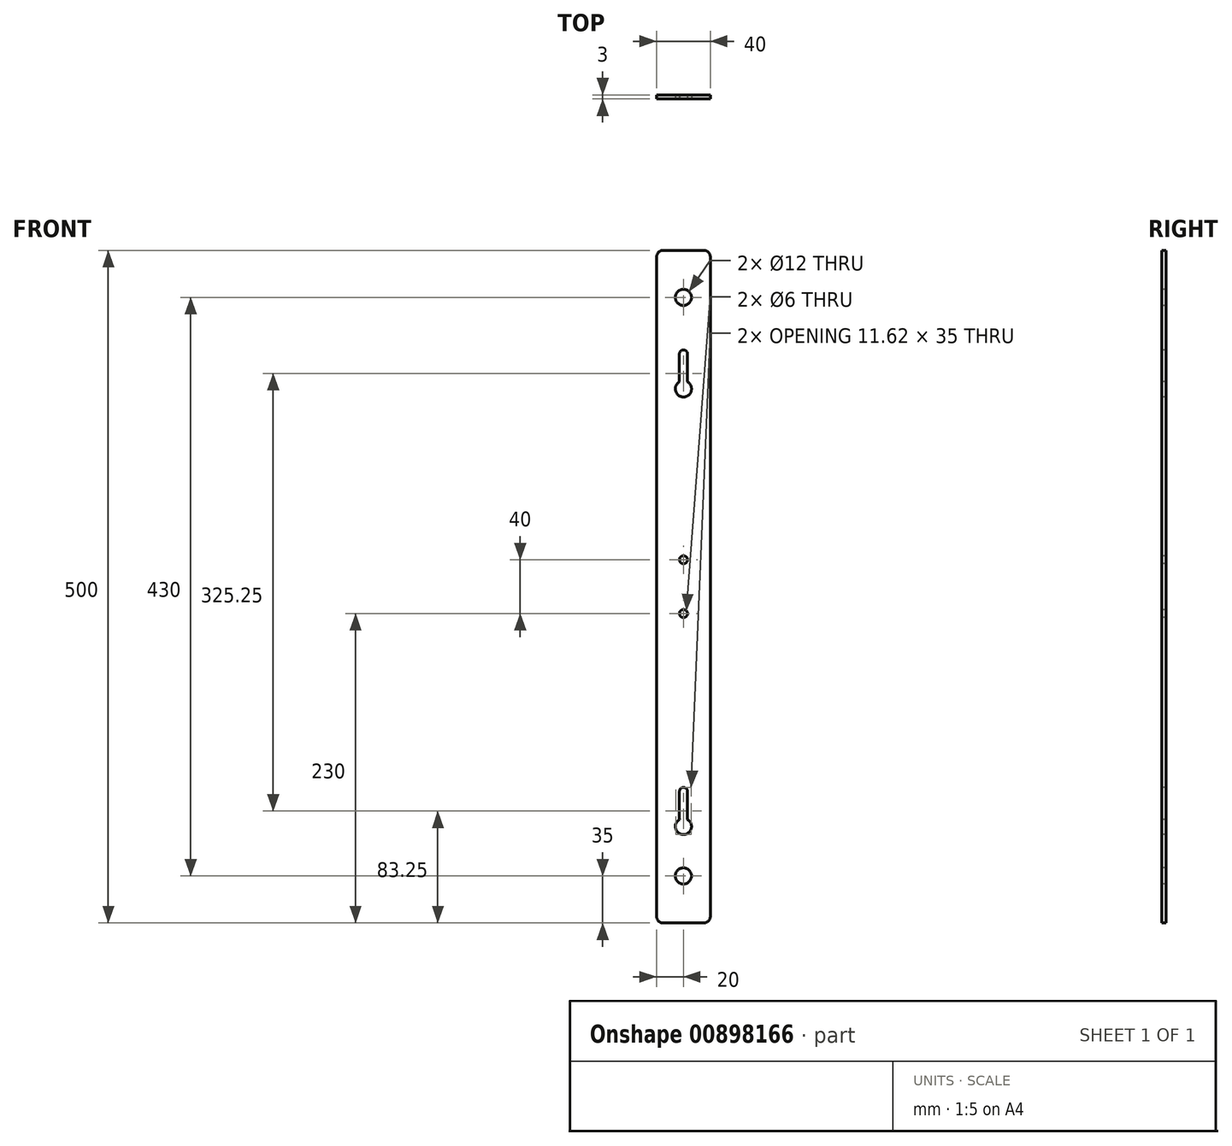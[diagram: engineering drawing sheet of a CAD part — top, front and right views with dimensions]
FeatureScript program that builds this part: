
annotation { "Feature Type Name" : "Feature", "Feature Type Description" : "" }
export const myFeature = defineFeature(function(context is Context, id is Id, definition is map)
    precondition{}
    {
        {
            var Q0;
            Q0=qCreatedBy(makeId("Front.planeOp"),FACE);
            var sketch = newSketch(context, id + "F0", { "sketchPlane" : qUnion([Q0])});
            skLineSegment(sketch, "E0.bottom", {"start": v(-20, 250) * mm, "end": v(20, 250) * mm});
            skLineSegment(sketch, "E0.top", {"start": v(-20, -250) * mm, "end": v(20, -250) * mm});
            skLineSegment(sketch, "E0.left", {"start": v(-20, 250) * mm, "end": v(-20, -250) * mm});
            skLineSegment(sketch, "E0.right", {"start": v(20, 250) * mm, "end": v(20, -250) * mm});
            skPoint(sketch, "E0.middle", {"position": v(0, 0) * mm});
            skSolve(sketch);
        }
        {
            var Q0;
            Q0 = qSketchRegion(id + "F0", true);
            extrude(context, id + "F1", {"entities" : qUnion([Q0]), "depth" : 3 * mm, "offsetDistance" : 25 * mm});
        }
        {
            var Q0;
            Q0=makeQuery(id+"F1.opExtrude","CAP_FACE",FACE,{"disambiguationData":[OSD([sQuery(id+"F0.wireOp",EDGE,"E0.bottom"),sQuery(id+"F0.wireOp",EDGE,"E0.top"),sQuery(id+"F0.wireOp",EDGE,"E0.left"),sQuery(id+"F0.wireOp",EDGE,"E0.right")])],"isStart":false});
            var sketch = newSketch(context, id + "F2", { "sketchPlane" : qUnion([Q0])});
            skPoint(sketch, "E1", {"position": v(0, 215) * mm});
            skPoint(sketch, "E2.MirrorP", {"position": v(0, -215) * mm});
            skSolve(sketch);
        }
        {
            var Q0;
            Q0=sQuery(id+"F2.wireOp",VERTEX,"E2.MirrorP");
            var Q1;
            Q1=sQuery(id+"F2.wireOp",VERTEX,"E1");
            var Q2;
            Q2=makeQuery(id+"F1.opExtrude","SWEPT_BODY",BODY,{"disambiguationData":[OSD([sQuery(id+"F0.wireOp",EDGE,"E0.bottom"),sQuery(id+"F0.wireOp",EDGE,"E0.top"),sQuery(id+"F0.wireOp",EDGE,"E0.left"),sQuery(id+"F0.wireOp",EDGE,"E0.right")])]});
            hole(context, id + "F3", {"style" : HoleStyle.SIMPLE, "endStyle" : HoleEndStyle.THROUGH, "holeDiameter" : 12 * mm, "majorDiameter" : 5 * mm, "isTappedThrough" : true, "tappedDepth" : 12 * mm, "tapClearance" : 3, "startFromSketch" : true, "locations" : qUnion([Q0, Q1]), "scope" : qUnion([Q2])});
        }
        {
            var Q0;
            Q0=makeQuery(id+"F1.opExtrude","CAP_FACE",FACE,{"disambiguationData":[OSD([sQuery(id+"F0.wireOp",EDGE,"E0.bottom"),sQuery(id+"F0.wireOp",EDGE,"E0.top"),sQuery(id+"F0.wireOp",EDGE,"E0.left"),sQuery(id+"F0.wireOp",EDGE,"E0.right")])],"isStart":false});
            var sketch = newSketch(context, id + "F4", { "sketchPlane" : qUnion([Q0])});
            skPoint(sketch, "E3", {"position": v(0, 147) * mm});
            skSolve(sketch);
        }
        {
            var Q0;
            Q0=sQuery(id+"F4.wireOp",VERTEX,"E3");
            var Q1;
            Q1=makeQuery(id+"F1.opExtrude","SWEPT_BODY",BODY,{"disambiguationData":[OSD([sQuery(id+"F0.wireOp",EDGE,"E0.bottom"),sQuery(id+"F0.wireOp",EDGE,"E0.top"),sQuery(id+"F0.wireOp",EDGE,"E0.left"),sQuery(id+"F0.wireOp",EDGE,"E0.right")])]});
            hole(context, id + "F5", {"style" : HoleStyle.SIMPLE, "endStyle" : HoleEndStyle.THROUGH, "holeDiameter" : 12 * mm, "majorDiameter" : 5 * mm, "isTappedThrough" : true, "tappedDepth" : 12 * mm, "tapClearance" : 3, "startFromSketch" : true, "locations" : qUnion([Q0]), "scope" : qUnion([Q1])});
        }
        {
            var Q0;
            Q0=makeQuery(id+"F1.opExtrude","CAP_FACE",FACE,{"disambiguationData":[OSD([sQuery(id+"F0.wireOp",EDGE,"E0.bottom"),sQuery(id+"F0.wireOp",EDGE,"E0.top"),sQuery(id+"F0.wireOp",EDGE,"E0.left"),sQuery(id+"F0.wireOp",EDGE,"E0.right")])],"isStart":false});
            var sketch = newSketch(context, id + "F6", { "sketchPlane" : qUnion([Q0])});
            skPoint(sketch, "E4", {"position": v(0, 215) * mm});
            skPoint(sketch, "E5.MirrorP", {"position": v(0, -215) * mm});
            skLineSegment(sketch, "E6", {"start": v(0, 153) * mm, "end": v(0, 173) * mm});
            skArc(sketch, "E7.0.startCap", {"start": v(3, 153) * mm, "mid": v(0, 150) * mm, "end": v(-3, 153) * mm});
            skArc(sketch, "E7.0.endCap", {"start": v(-3, 173) * mm, "mid": v(0, 176) * mm, "end": v(3, 173) * mm});
            skLineSegment(sketch, "E7.0.left", {"start": v(-3, 153) * mm, "end": v(-3, 173) * mm});
            skLineSegment(sketch, "E7.0.right", {"start": v(3, 153) * mm, "end": v(3, 173) * mm});
            skPoint(sketch, "E8", {"position": v(0, -178.25) * mm});
            skSolve(sketch);
        }
        {
            var Q0;
            Q0 = qSketchRegion(id + "F6", true);
            extrude(context, id + "F7", {"entities" : qUnion([Q0]), "operationType" : NewBodyOperationType.REMOVE, "oppositeDirection" : true, "depth" : 6 * mm, "offsetDistance" : 25 * mm});
        }
        {
            var Q0;
            Q0=sQuery(id+"F6.wireOp",VERTEX,"E8");
            var Q1;
            Q1=makeQuery(id+"F1.opExtrude","SWEPT_BODY",BODY,{"disambiguationData":[OSD([sQuery(id+"F0.wireOp",EDGE,"E0.bottom"),sQuery(id+"F0.wireOp",EDGE,"E0.top"),sQuery(id+"F0.wireOp",EDGE,"E0.left"),sQuery(id+"F0.wireOp",EDGE,"E0.right")])]});
            hole(context, id + "F8", {"style" : HoleStyle.SIMPLE, "endStyle" : HoleEndStyle.THROUGH, "holeDiameter" : 12 * mm, "majorDiameter" : 5 * mm, "isTappedThrough" : true, "tappedDepth" : 12 * mm, "tapClearance" : 3, "startFromSketch" : true, "locations" : qUnion([Q0]), "scope" : qUnion([Q1])});
        }
        {
            var Q0;
            Q0=makeQuery(id+"F1.opExtrude","CAP_FACE",FACE,{"disambiguationData":[OSD([sQuery(id+"F0.wireOp",EDGE,"E0.bottom"),sQuery(id+"F0.wireOp",EDGE,"E0.top"),sQuery(id+"F0.wireOp",EDGE,"E0.left"),sQuery(id+"F0.wireOp",EDGE,"E0.right")])],"isStart":false});
            var sketch = newSketch(context, id + "F9", { "sketchPlane" : qUnion([Q0])});
            skLineSegment(sketch, "E9", {"start": v(0, -172.25) * mm, "end": v(0, -152.25) * mm});
            skArc(sketch, "E10.0.startCap", {"start": v(3, -172.25) * mm, "mid": v(0, -175.25) * mm, "end": v(-3, -172.25) * mm});
            skArc(sketch, "E10.0.endCap", {"start": v(-3, -152.25) * mm, "mid": v(0, -149.25) * mm, "end": v(3, -152.25) * mm});
            skLineSegment(sketch, "E10.0.left", {"start": v(-3, -172.25) * mm, "end": v(-3, -152.25) * mm});
            skLineSegment(sketch, "E10.0.right", {"start": v(3, -172.25) * mm, "end": v(3, -152.25) * mm});
            skSolve(sketch);
        }
        {
            var Q0;
            Q0 = qSketchRegion(id + "F9", true);
            extrude(context, id + "F10", {"entities" : qUnion([Q0]), "operationType" : NewBodyOperationType.REMOVE, "oppositeDirection" : true, "depth" : 6 * mm, "offsetDistance" : 25 * mm});
        }
        {
            var Q0;
            Q0=makeQuery(id+"F1.opExtrude","CAP_FACE",FACE,{"disambiguationData":[OSD([sQuery(id+"F0.wireOp",EDGE,"E0.bottom"),sQuery(id+"F0.wireOp",EDGE,"E0.top"),sQuery(id+"F0.wireOp",EDGE,"E0.left"),sQuery(id+"F0.wireOp",EDGE,"E0.right")])],"isStart":false});
            var sketch = newSketch(context, id + "F11", { "sketchPlane" : qUnion([Q0])});
            skPoint(sketch, "E11", {"position": v(0, 20) * mm});
            skPoint(sketch, "E12.MirrorP", {"position": v(0, -20) * mm});
            skSolve(sketch);
        }
        {
            var Q0;
            Q0=sQuery(id+"F11.wireOp",VERTEX,"E11");
            var Q1;
            Q1=sQuery(id+"F11.wireOp",VERTEX,"E12.MirrorP");
            var Q2;
            Q2=makeQuery(id+"F1.opExtrude","SWEPT_BODY",BODY,{"disambiguationData":[OSD([sQuery(id+"F0.wireOp",EDGE,"E0.bottom"),sQuery(id+"F0.wireOp",EDGE,"E0.top"),sQuery(id+"F0.wireOp",EDGE,"E0.left"),sQuery(id+"F0.wireOp",EDGE,"E0.right")])]});
            hole(context, id + "F12", {"style" : HoleStyle.SIMPLE, "endStyle" : HoleEndStyle.THROUGH, "holeDiameter" : 6 * mm, "majorDiameter" : 5 * mm, "isTappedThrough" : true, "tappedDepth" : 12 * mm, "tapClearance" : 3, "startFromSketch" : true, "locations" : qUnion([Q0, Q1]), "scope" : qUnion([Q2])});
        }
        {
            var Q0;
            Q0=makeQuery(id+"F1.opExtrude","SWEPT_EDGE",EDGE,{"disambiguationData":[OSD([sQuery(id+"F0.wireOp",EDGE,"E0.top"),sQuery(id+"F0.wireOp",EDGE,"E0.left")])]});
            var Q1;
            Q1=makeQuery(id+"F1.opExtrude","SWEPT_EDGE",EDGE,{"disambiguationData":[OSD([sQuery(id+"F0.wireOp",EDGE,"E0.top"),sQuery(id+"F0.wireOp",EDGE,"E0.right")])]});
            var Q2;
            Q2=makeQuery(id+"F1.opExtrude","SWEPT_EDGE",EDGE,{"disambiguationData":[OSD([sQuery(id+"F0.wireOp",EDGE,"E0.bottom"),sQuery(id+"F0.wireOp",EDGE,"E0.right")])]});
            var Q3;
            Q3=makeQuery(id+"F1.opExtrude","SWEPT_EDGE",EDGE,{"disambiguationData":[OSD([sQuery(id+"F0.wireOp",EDGE,"E0.bottom"),sQuery(id+"F0.wireOp",EDGE,"E0.left")])]});
            fillet(context, id + "F13", {"entities" : qUnion([Q0, Q1, Q2, Q3]), "radius" : 5 * mm, "tangentPropagation" : true, "allowEdgeOverflow" : false});
        }
    });
